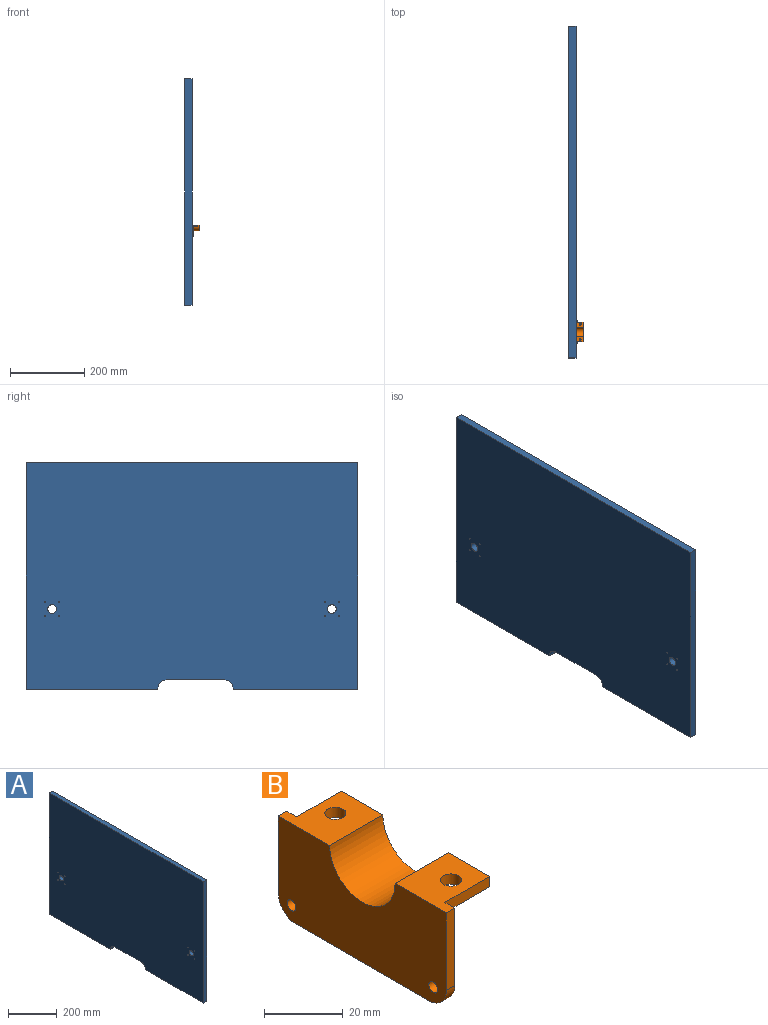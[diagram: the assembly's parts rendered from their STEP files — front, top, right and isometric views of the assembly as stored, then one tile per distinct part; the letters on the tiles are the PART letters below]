
ASSEMBLY  parts=2 mates=1
PART A: 20 faces, bbox 19.1x892.8x609.6 mm
  f0: plane 354.33x19.05mm, normal (0,0,-1), area 6750mm2, adj f13,f15,f16,f19
  f1: plane 335.28x19.05mm, normal (0,0,-1), area 6387.1mm2, adj f2,f15,f16,f18
  f2: plane 609.6x19.05mm, normal (0,-1,0), area 11612.9mm2, adj f1,f3,f15,f16
  f3: plane 892.81x19.05mm, normal (0,0,1), area 17008mm2, adj f2,f13,f15,f16
  f4: cylinder r=1.59mm len=19.05mm, axis (1,0,0), area 190mm2, adj f15,f16
  f5: cylinder r=1.59mm len=19.05mm, axis (1,0,0), area 190mm2, adj f15,f16
  f6: cylinder r=1.59mm len=19.05mm, axis (1,0,0), area 190mm2, adj f15,f16
  f7: cylinder r=1.59mm len=19.05mm, axis (1,0,0), area 190mm2, adj f15,f16
  f8: cylinder r=1.59mm len=19.05mm, axis (1,0,0), area 190mm2, adj f15,f16
  f9: cylinder r=11.71mm len=23.42mm, axis (1,0,0), area 1401.6mm2, adj f15,f16
  f10: cylinder r=11.71mm len=23.42mm, axis (1,0,0), area 1401.6mm2, adj f15,f16
  f11: cylinder r=1.59mm len=19.05mm, axis (1,0,0), area 190mm2, adj f15,f16
  f12: cylinder r=1.59mm len=19.05mm, axis (1,0,0), area 190mm2, adj f15,f16
  f13: plane 609.6x19.05mm, normal (0,1,0), area 11612.9mm2, adj f0,f3,f15,f16
  f14: cylinder r=1.59mm len=19.05mm, axis (1,0,0), area 190mm2, adj f15,f16
  f15: plane 892.81x609.6mm, normal (-1,0,0), area 538447.8mm2, adj f0,f1,f2,f3,f4,f5,f6,f7
  f16: plane 892.81x609.6mm, normal (1,0,0), area 538447.8mm2, adj f0,f1,f2,f3,f4,f5,f6,f7
  f17: plane 152.4x19.05mm, normal (0,0,-1), area 2903.2mm2, adj f15,f16,f18,f19
  f18: cylinder r=25.4mm len=25.4mm, axis (1,0,0), area 760.1mm2, adj f1,f15,f16,f17
  f19: cylinder r=25.4mm len=25.4mm, axis (1,0,0), area 760.1mm2, adj f0,f15,f16,f17
PART B: 20 faces, bbox 19.1x60.2x30.4 mm
  f0: cylinder r=15.31mm len=29.95mm, axis (-1,0,0), area 669.3mm2, adj f1,f13,f14,f17
  f1: plane 60.17x30.36mm, normal (1,0,0), area 1353.2mm2, adj f0,f2,f3,f4,f5,f6,f7,f8
  f2: plane 24.01x3mm, normal (0,1,0), area 72mm2, adj f1,f3,f10,f11
  f3: plane 19.05x18.37mm, normal (0,0,1), area 270.6mm2, adj f1,f2,f11,f12,f13,f18,f19
  f4: plane 19.05x18.37mm, normal (0,0,1), area 270.6mm2, adj f1,f5,f11,f12,f13,f15,f16
  f5: plane 24.01x3mm, normal (0,-1,0), area 72mm2, adj f1,f4,f6,f11
  f6: cylinder r=6.35mm len=6.35mm, axis (-1,0,0), area 29.9mm2, adj f1,f5,f7,f11
  f7: plane 47.47x3mm, normal (0,0,-1), area 142.4mm2, adj f1,f6,f10,f11
  f8: cylinder r=1.59mm len=3.18mm, axis (-1,0,0), area 29.9mm2, adj f1,f11
  f9: cylinder r=1.59mm len=3.18mm, axis (-1,0,0), area 29.9mm2, adj f1,f11
  f10: cylinder r=6.35mm len=6.35mm, axis (-1,0,0), area 29.9mm2, adj f1,f2,f7,f11
  f11: plane 60.17x30.36mm, normal (-1,0,0), area 1577.9mm2, adj f2,f3,f4,f5,f6,f7,f8,f9
  f12: cylinder r=11.71mm len=23.42mm, axis (-1,0,0), area 700.8mm2, adj f3,f4,f11,f13
  f13: plane 53.05x15.31mm, normal (1,0,0), area 224.7mm2, adj f0,f3,f4,f12,f14,f15,f17,f18
  f14: plane 16.05x11.55mm, normal (0,0,-1), area 163mm2, adj f0,f1,f13,f15,f16
  f15: plane 16.05x3.18mm, normal (0,-1,0), area 51mm2, adj f1,f4,f13,f14
  f16: cylinder r=2.67mm len=5.34mm, axis (0,0,1), area 53.2mm2, adj f4,f14
  f17: plane 16.05x11.55mm, normal (0,0,-1), area 163mm2, adj f0,f1,f13,f18,f19
  f18: plane 16.05x3.18mm, normal (0,1,0), area 51mm2, adj f1,f3,f13,f17
  f19: cylinder r=2.67mm len=5.34mm, axis (0,0,1), area 53.2mm2, adj f3,f17
PLACE A t=(608.33,436.88,76.2)mm
PLACE B t=(0,-6.35,-6.35)mm
MATE revolute A.f9 <-> B.f0  axis (1,0,0) through (19.05,69.85,215.9)mm
